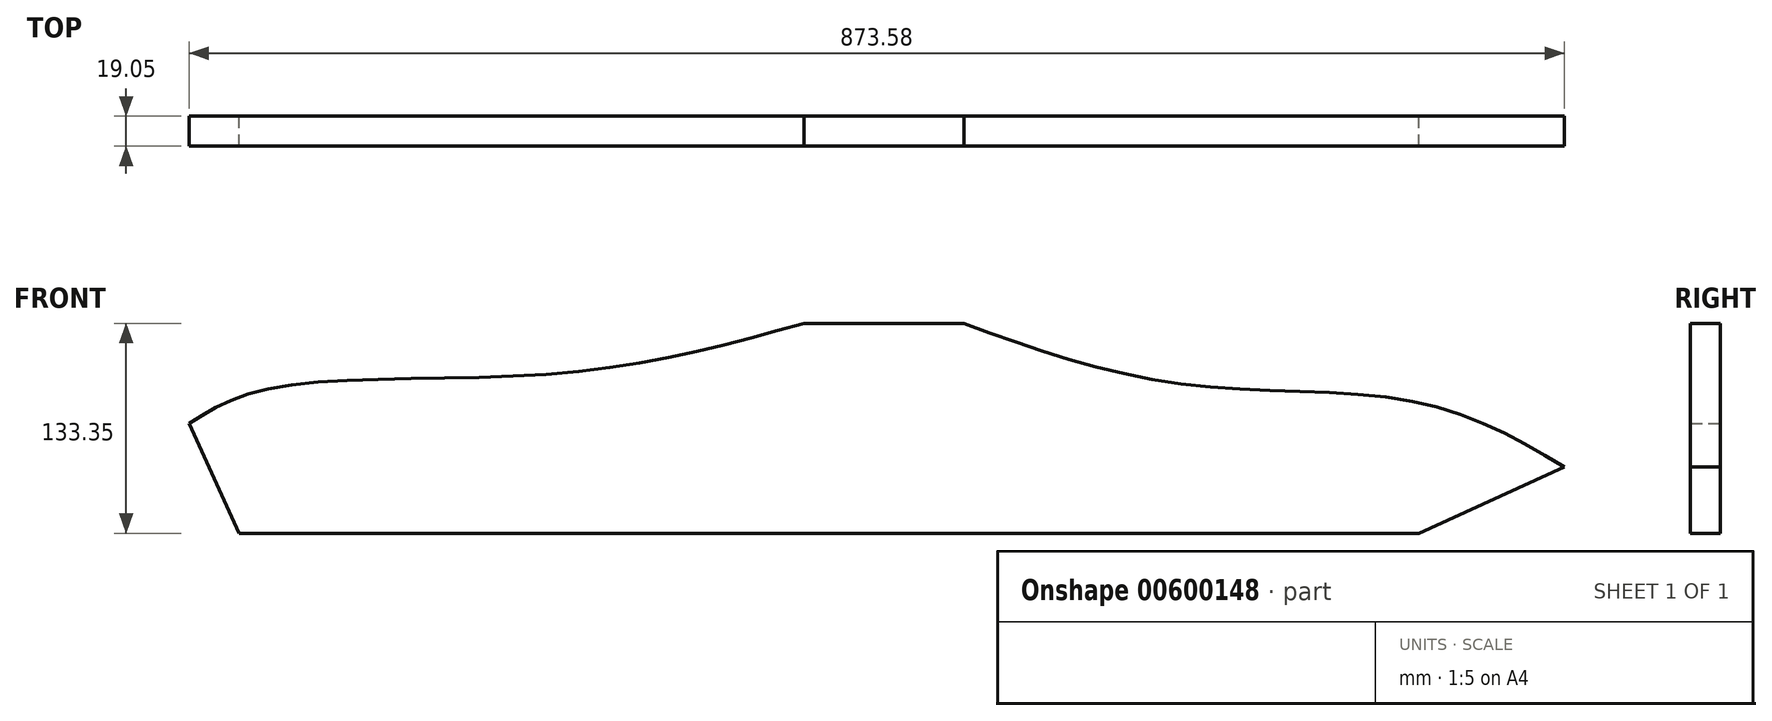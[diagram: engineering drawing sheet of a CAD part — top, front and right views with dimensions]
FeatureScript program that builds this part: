
annotation { "Feature Type Name" : "Feature", "Feature Type Description" : "" }
export const myFeature = defineFeature(function(context is Context, id is Id, definition is map)
    precondition{}
    {
        {
            var Q0;
            Q0=qCreatedBy(makeId("Front.planeOp"),FACE);
            var sketch = newSketch(context, id + "F0", { "sketchPlane" : qUnion([Q0])});
            skLineSegment(sketch, "E0.bottom", {"start": v(-785.27, 120) * mm, "end": v(103.73, 120) * mm, "construction": true});
            skLineSegment(sketch, "E1", {"start": v(-785.27, 100.95) * mm, "end": v(-759.87, 100.95) * mm});
            skLineSegment(sketch, "E2", {"start": v(78.33, -32.75) * mm, "end": v(78.33, 100.95) * mm, "construction": true});
            skLineSegment(sketch, "E3", {"start": v(-759.87, -32.75) * mm, "end": v(-759.87, 51.53) * mm, "construction": true});
            skLineSegment(sketch, "E4", {"start": v(-785.27, 43.8) * mm, "end": v(103.73, 43.8) * mm, "construction": true});
            skLineSegment(sketch, "E5", {"start": v(-293.15, 100.95) * mm, "end": v(-293.15, -32.75) * mm, "construction": true});
            skLineSegment(sketch, "E6", {"start": v(-394.75, 100.95) * mm, "end": v(-394.75, -32.75) * mm, "construction": true});
            skLineSegment(sketch, "E7", {"start": v(-753.44, -32.4) * mm, "end": v(-785.27, 37.45) * mm});
            skLineSegment(sketch, "E8", {"start": v(-785.27, 69.2) * mm, "end": v(103.73, 69.2) * mm, "construction": true});
            skLineSegment(sketch, "E9", {"start": v(103.73, 18.4) * mm, "end": v(-785.27, 18.4) * mm, "construction": true});
            skLineSegment(sketch, "E10", {"start": v(-4.14, -32.4) * mm, "end": v(88.3, 9.74) * mm});
            skFitSpline(sketch, "E11", {"points": [v(-293.15, 100.95) * mm, v(-154.93, 62.48) * mm, v(-4.14, 50.62) * mm, v(88.3, 9.74) * mm], "startDerivative": vector(376.3, -138.22) * mm, "endDerivative": vector(287.35, -171.23) * mm});
            skFitSpline(sketch, "E12", {"points": [v(-785.27, 37.45) * mm, v(-732.77, 59.87) * mm, v(-550.02, 69.2) * mm, v(-394.75, 100.95) * mm], "startDerivative": vector(188.8, 118.04) * mm, "endDerivative": vector(386.27, 107.61) * mm});
            skLineSegment(sketch, "E13.trimOffspring", {"start": v(-394.75, 100.95) * mm, "end": v(-293.15, 100.95) * mm});
            skLineSegment(sketch, "E14.trimOffspring", {"start": v(-759.87, 69.2) * mm, "end": v(-759.87, 100.95) * mm, "construction": true});
            skLineSegment(sketch, "E15.trimOffspring", {"start": v(-753.44, -32.4) * mm, "end": v(-4.14, -32.4) * mm});
            skSolve(sketch);
        }
        {
            var Q0;
            Q0 = qSketchRegion(id + "F0", true);
            extrude(context, id + "F1", {"entities" : qUnion([Q0]), "depth" : 19.05 * mm, "offsetDistance" : 25.4 * mm});
        }
    });
